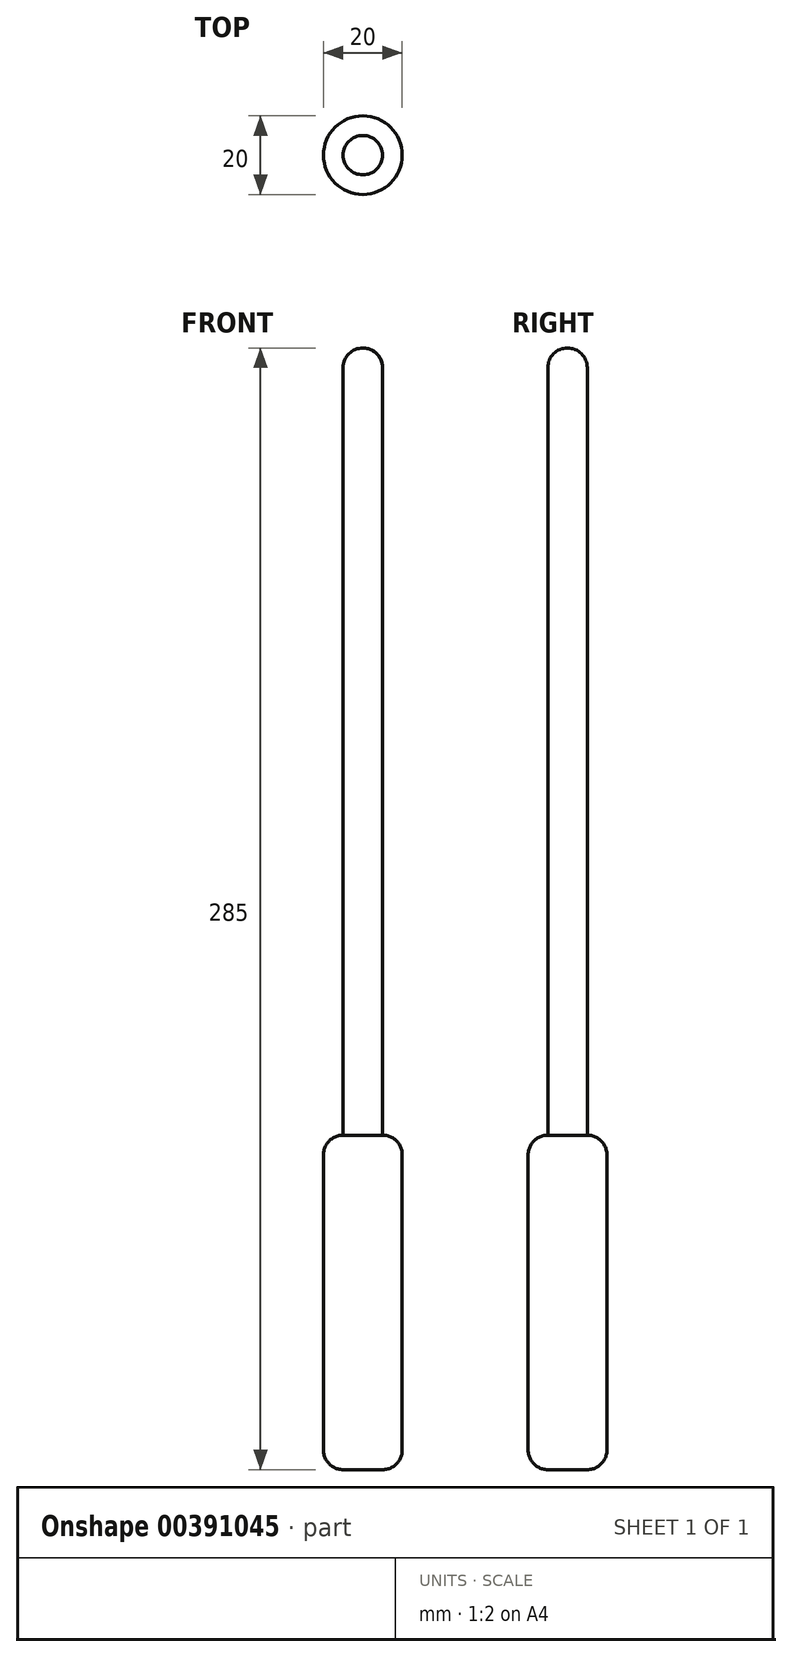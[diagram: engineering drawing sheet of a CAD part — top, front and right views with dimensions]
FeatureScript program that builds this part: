
annotation { "Feature Type Name" : "Feature", "Feature Type Description" : "" }
export const myFeature = defineFeature(function(context is Context, id is Id, definition is map)
    precondition{}
    {
        {
            var Q0;
            Q0=qCreatedBy(makeId("Top.planeOp"),FACE);
            var sketch = newSketch(context, id + "F0", { "sketchPlane" : qUnion([Q0])});
            skCircle(sketch, "E0", {"center": v(0, 0) * mm, "radius": 5 * mm});
            skSolve(sketch);
        }
        {
            var Q0;
            Q0=makeQuery(id+"F0.imprint","IMPRINT",FACE,{"disambiguationData":[TD([[makeQuery(id+"F0.imprint","IMPRINT",EDGE,{"derivedFrom":sQuery(id+"F0.wireOp",EDGE,"E0")}),1.0]])]});
            extrude(context, id + "F1", {"entities" : qUnion([Q0]), "depth" : 200 * mm});
        }
        {
            var Q0;
            Q0=makeQuery(id+"F1.opExtrude","CAP_FACE",FACE,{"disambiguationData":[OSD([sQuery(id+"F0.wireOp",EDGE,"E0")])],"isStart":true});
            var sketch = newSketch(context, id + "F2", { "sketchPlane" : qUnion([Q0])});
            skCircle(sketch, "E1", {"center": v(0, 0) * mm, "radius": 10 * mm});
            skSolve(sketch);
        }
        {
            var Q0;
            Q0=makeQuery(id+"F2.imprint","IMPRINT",FACE,{"disambiguationData":[TD([[makeQuery(id+"F2.imprint","IMPRINT",EDGE,{"derivedFrom":sQuery(id+"F2.wireOp",EDGE,"E1")}),1.0]])]});
            var Q1;
            Q1=makeQuery(id+"F2.imprint","IMPRINT",FACE,{"disambiguationData":[TD([[makeQuery(id+"F2.imprint","IMPRINT",EDGE,{"derivedFrom":makeQuery(id+"F1.opExtrude","CAP_EDGE",EDGE,{"disambiguationData":[OSD([sQuery(id+"F0.wireOp",EDGE,"E0")])],"isStart":true})}),-1.0]])]});
            extrude(context, id + "F3", {"entities" : qUnion([Q0, Q1]), "operationType" : NewBodyOperationType.ADD, "depth" : 85 * mm});
        }
        {
            var Q0;
            Q0=makeQuery(id+"F3.opExtrude","CAP_EDGE",EDGE,{"disambiguationData":[OSD([sQuery(id+"F2.wireOp",EDGE,"E1")])],"isStart":true});
            var Q1;
            Q1=makeQuery(id+"F3.opExtrude","CAP_EDGE",EDGE,{"disambiguationData":[OSD([sQuery(id+"F2.wireOp",EDGE,"E1")])],"isStart":false});
            fillet(context, id + "F4", {"entities" : qUnion([Q0, Q1]), "radius" : 5 * mm, "tangentPropagation" : true, "allowEdgeOverflow" : false});
        }
        {
            var Q0;
            Q0=makeQuery(id+"F1.opExtrude","CAP_EDGE",EDGE,{"disambiguationData":[OSD([sQuery(id+"F0.wireOp",EDGE,"E0")])],"isStart":false});
            fillet(context, id + "F5", {"entities" : qUnion([Q0]), "radius" : 5 * mm, "tangentPropagation" : true, "allowEdgeOverflow" : false});
        }
        {
            var Q0;
            Q0=qCreatedBy(makeId("Right.planeOp"),FACE);
            cPlane(context, id + "F6", {"entities" : qUnion([Q0]), "cplaneType" : CPlaneType.OFFSET, "offset" : 5 * mm, "width" : 150 * mm, "height" : 150 * mm});
        }
    });
